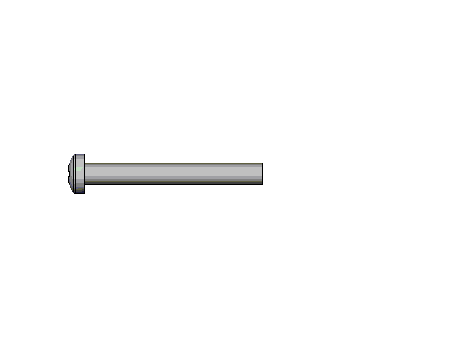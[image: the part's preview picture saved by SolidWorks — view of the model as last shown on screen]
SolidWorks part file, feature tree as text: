
SOLIDWORKS PART (.sldprt)
format: sldprt  version: not decoded by parser v0  size: 185,344 bytes
history: native  units: mm
features: plane x4, sketch x4, cut_revolve x4, material x1, revolve x1, thread x1, pattern_circular x1, pattern_linear x1 (+11 scaffold rows collapsed; 1 parser-record rows omitted)
feature tree (29):
  parser-record x1  (decoder bookkeeping rows leaked as tree rows — omitted from the tree; the rows remain in map.json)
  scaffold x11  (default folders/planes/origin — collapsed)
  material  "Material <not specified>"
  plane  "Plane1"
  plane  "Plane2"
  plane  "Plane3"
  sketch  "BodySke"  dims[c1.Head_fillet_rad=3.6322mm c1.Head_crown_rad=5.0mm c2.Head_fillet_rad=0.36mm c2.D1=~7.099516mm c2.Head_ang=85.0deg c2.Oval_ht=2.3876mm c2.Head_ht=6.1976mm c2.Diameter=3.0mm c2.Length=76.2mm c2.Head_dia=20.0152mm c3.Head_dia=15.3924mm c3.Head_ht=8.509mm c3.Length=25.0mm c3.Head_side_ht=6.1722mm c4.Head_ht=5.1562mm c4.Head_dia=18.4912mm c5.Head_ht=2.4mm c5.Head_dia=5.6mm c5.Advance=0.5mm c5.Thread_nom=25.0mm c5.Thread_lim=~37.30625mm]
  revolve  "Base-Revolve"  [1 undecoded]
  thread  "ThreadCosmetic"  Diameter=24.5mm Thread_length=24.5mm Thread_minor=2.439mm Head_dia=5.6mm  [1 undecoded]
  sketch  "Sketch3"  dims[Cross_dia=2.9mm D1=1.45mm Cross_width=0.74mm D2=0.37mm]
  plane  "Plane4"  Offset=1.76mm Cross_depth=1.76mm
  sketch  "Sketch4"  dims[D1=0.37mm D2=0.37mm D3=0.185mm D4=0.185mm]
  pattern_circular  "CirPattern1"  Count=2 Angle=90deg
  sketch  "ThdSchSke"  dims[c1.Thread_minor=~1.03886mm c1.Diameter=~1.413535mm c1.Start=~0.988134mm c1.D4=~4.446753mm c1.Vee=60.0deg c2.Thread_minor=~1.03886mm c2.Start=~2.540025mm c2.D1=~0.108159mm c2.D2=~0.108159mm c3.D1=~0.216319mm c3.SideAngle=55.0deg c3.D2=~0.216319mm c3.VeeAngle=70.0deg c3.Thread_minor=2.439mm c3.Overcut=3.75mm c3.Diameter=3.0mm c3.D6=~8.326268mm c4.D1=~8.326268mm c5.D1=90.0deg c5.Start=11.1125mm c6.Start=~44.450025mm c7.Start=2.9mm]
  cut_revolve  "ThreadSchematic"  Angle=360deg
  pattern_linear  "ThdSchPat"  Count1=50 Count2=1 Spacing1=0.5mm Spacing2=50mm Num_threads=50 Advance=0.5mm
  cut_revolve  "ConfigurationName"  CopiedFlag=1  [1 undecoded]
  cut_revolve  "PartNumberID"  [1 undecoded]
  cut_revolve  "ConfigurationName"  CopiedFlag=0  [1 undecoded]
decode coverage: 10 of 12 modeling features carry decoded parameters
note: ~ marks probable driven/reference dimensions
note: 5 parameter values undecoded
summary: no parameter record found for 4 features
note: suppression state not decoded; provenance and decode notes live in map.json
